# Revit family: ALM_клапан
name_source: partatom
category: Арматура воздуховодов
revit_build: Autodesk Revit 2014 (Build: 20140709_2115(x64)
units: mm (PartAtom-declared; Revit-internal decimal feet)

## types (198) — shared parameters
Aef = 0.82 м²
W = 70 мм
Материал = Оцинкованная сталь (INPLAST)
УГО = УГО(INPLAST)

## per-type parameters (varying)
| type | A | B | Вес | Тип привода |
| ALM-100x105-T1 | 100 мм | 105 мм | 0.7 | 1 |
| ALM-100x155-T1 | 100 мм | 155 мм | 0.9 | 1 |
| ALM-100x205-T1 | 100 мм | 205 мм | 1.2 | 1 |
| ALM-100x255-T1 | 100 мм | 255 мм | 1.4 | 1 |
| ALM-100x305-T1 | 100 мм | 305 мм | 1.6 | 1 |
| ALM-100x355-T1 | 100 мм | 355 мм | 1.9 | 1 |
| ALM-100x405-T1 | 100 мм | 405 мм | 2.1 | 1 |
| ALM-100x455-T1 | 100 мм | 455 мм | 2.4 | 1 |
| ALM-100x505-T1 | 100 мм | 505 мм | 2.6 | 1 |
| ALM-100x555-T1 | 100 мм | 555 мм | 2.9 | 1 |
| ALM-100x605-T1 | 100 мм | 605 мм | 3.1 | 1 |
| ALM-200x105-T1 | 200 мм | 105 мм | 0.8 | 1 |
| ALM-200x155-T1 | 200 мм | 155 мм | 1.1 | 1 |
| ALM-200x205-T1 | 200 мм | 205 мм | 1.4 | 1 |
| ALM-200x255-T1 | 200 мм | 255 мм | 1.7 | 1 |
| ALM-200x305-T1 | 200 мм | 305 мм | 1.9 | 1 |
| ALM-200x355-T1 | 200 мм | 355 мм | 2.2 | 1 |
| ALM-200x405-T1 | 200 мм | 405 мм | 2.5 | 1 |
| ALM-200x455-T1 | 200 мм | 455 мм | 2.8 | 1 |
| ALM-200x505-T1 | 200 мм | 505 мм | 3.1 | 1 |
| ALM-200x555-T1 | 200 мм | 555 мм | 3.4 | 1 |
| ALM-200x605-T1 | 200 мм | 605 мм | 3.7 | 1 |
| ALM-300x105-T1 | 300 мм | 105 мм | 1 | 1 |
| ALM-300x155-T1 | 300 мм | 155 мм | 1.3 | 1 |
| ALM-300x205-T1 | 300 мм | 205 мм | 1.6 | 1 |
| ALM-300x255-T1 | 300 мм | 255 мм | 1.9 | 1 |
| ALM-300x305-T1 | 300 мм | 305 мм | 2.3 | 1 |
| ALM-300x355-T1 | 300 мм | 355 мм | 2.6 | 1 |
| ALM-300x405-T1 | 300 мм | 405 мм | 2.9 | 1 |
| ALM-300x455-T1 | 300 мм | 455 мм | 3.3 | 1 |
| ALM-300x505-T1 | 300 мм | 505 мм | 3.6 | 1 |
| ALM-300x555-T1 | 300 мм | 555 мм | 3.9 | 1 |
| ALM-300x605-T1 | 300 мм | 605 мм | 4.2 | 1 |
| ALM-400x105-T1 | 400 мм | 105 мм | 1.1 | 1 |
| ALM-400x155-T1 | 400 мм | 155 мм | 1.5 | 1 |
| ALM-400x205-T1 | 400 мм | 205 мм | 1.9 | 1 |
| ALM-400x255-T1 | 400 мм | 255 мм | 2.2 | 1 |
| ALM-400x305-T1 | 400 мм | 305 мм | 2.6 | 1 |
| ALM-400x355-T1 | 400 мм | 355 мм | 2.9 | 1 |
| ALM-400x405-T1 | 400 мм | 405 мм | 3.3 | 1 |
| ALM-400x455-T1 | 400 мм | 455 мм | 3.7 | 1 |
| ALM-400x505-T1 | 400 мм | 505 мм | 4.1 | 1 |
| ALM-400x555-T1 | 400 мм | 555 мм | 4.4 | 1 |
| ALM-400x605-T1 | 400 мм | 605 мм | 4.8 | 1 |
| ALM-500x105-T1 | 500 мм | 105 мм | 1.3 | 1 |
| ALM-500x155-T1 | 500 мм | 155 мм | 1.7 | 1 |
| ALM-500x205-T1 | 500 мм | 205 мм | 2.1 | 1 |
| ALM-500x255-T1 | 500 мм | 255 мм | 2.5 | 1 |
| ALM-500x305-T1 | 500 мм | 305 мм | 2.9 | 1 |
| ALM-500x355-T1 | 500 мм | 355 мм | 3.3 | 1 |
| ALM-500x405-T1 | 500 мм | 405 мм | 3.7 | 1 |
| ALM-500x455-T1 | 500 мм | 455 мм | 4.1 | 1 |
| ALM-500x505-T1 | 500 мм | 505 мм | 4.5 | 1 |
| ALM-500x555-T1 | 500 мм | 555 мм | 4.9 | 1 |
| ALM-500x605-T1 | 500 мм | 605 мм | 5.3 | 1 |
| ALM-600x105-T1 | 600 мм | 105 мм | 1.4 | 1 |
| ALM-600x155-T1 | 600 мм | 155 мм | 1.9 | 1 |
| ALM-600x205-T1 | 600 мм | 205 мм | 2.3 | 1 |
| ALM-600x255-T1 | 600 мм | 255 мм | 2.8 | 1 |
| ALM-600x305-T1 | 600 мм | 305 мм | 3.2 | 1 |
| ALM-600x355-T1 | 600 мм | 355 мм | 3.7 | 1 |
| ALM-600x405-T1 | 600 мм | 405 мм | 4.1 | 1 |
| ALM-600x455-T1 | 600 мм | 455 мм | 4.6 | 1 |
| ALM-600x505-T1 | 600 мм | 505 мм | 5 | 1 |
| ALM-600x555-T1 | 600 мм | 555 мм | 5.5 | 1 |
| ALM-600x605-T1 | 600 мм | 605 мм | 5.9 | 1 |
| ALM-100x105-T2 | 100 мм | 105 мм | 0.7 | 2 |
| ALM-100x155-T2 | 100 мм | 155 мм | 0.9 | 2 |
| ALM-100x205-T2 | 100 мм | 205 мм | 1.2 | 2 |
| ALM-100x255-T2 | 100 мм | 255 мм | 1.4 | 2 |
| ALM-100x305-T2 | 100 мм | 305 мм | 1.6 | 2 |
| ALM-100x355-T2 | 100 мм | 355 мм | 1.9 | 2 |
| ALM-100x405-T2 | 100 мм | 405 мм | 2.1 | 2 |
| ALM-100x455-T2 | 100 мм | 455 мм | 2.4 | 2 |
| ALM-100x505-T2 | 100 мм | 505 мм | 2.6 | 2 |
| ALM-100x555-T2 | 100 мм | 555 мм | 2.9 | 2 |
| ALM-100x605-T2 | 100 мм | 605 мм | 3.1 | 2 |
| ALM-200x105-T2 | 200 мм | 105 мм | 0.8 | 2 |
| ALM-200x155-T2 | 200 мм | 155 мм | 1.1 | 2 |
| ALM-200x205-T2 | 200 мм | 205 мм | 1.4 | 2 |
| ALM-200x255-T2 | 200 мм | 255 мм | 1.7 | 2 |
| ALM-200x305-T2 | 200 мм | 305 мм | 1.9 | 2 |
| ALM-200x355-T2 | 200 мм | 355 мм | 2.2 | 2 |
| ALM-200x405-T2 | 200 мм | 405 мм | 2.5 | 2 |
| ALM-200x455-T2 | 200 мм | 455 мм | 2.8 | 2 |
| ALM-200x505-T2 | 200 мм | 505 мм | 3.1 | 2 |
| ALM-200x555-T2 | 200 мм | 555 мм | 3.4 | 2 |
| ALM-200x605-T2 | 200 мм | 605 мм | 3.7 | 2 |
| ALM-300x105-T2 | 300 мм | 105 мм | 1 | 2 |
| ALM-300x155-T2 | 300 мм | 155 мм | 1.3 | 2 |
| ALM-300x205-T2 | 300 мм | 205 мм | 1.6 | 2 |
| ALM-300x255-T2 | 300 мм | 255 мм | 1.9 | 2 |
| ALM-300x305-T2 | 300 мм | 305 мм | 2.3 | 2 |
| ALM-300x355-T2 | 300 мм | 355 мм | 2.6 | 2 |
| ALM-300x405-T2 | 300 мм | 405 мм | 2.9 | 2 |
| ALM-300x455-T2 | 300 мм | 455 мм | 3.3 | 2 |
| ALM-300x505-T2 | 300 мм | 505 мм | 3.6 | 2 |
| ALM-300x555-T2 | 300 мм | 555 мм | 3.9 | 2 |
| ALM-300x605-T2 | 300 мм | 605 мм | 4.2 | 2 |
| ALM-400x105-T2 | 400 мм | 105 мм | 1.1 | 2 |
| ALM-400x155-T2 | 400 мм | 155 мм | 1.5 | 2 |
| ALM-400x205-T2 | 400 мм | 205 мм | 1.9 | 2 |
| ALM-400x255-T2 | 400 мм | 255 мм | 2.2 | 2 |
| ALM-400x305-T2 | 400 мм | 305 мм | 2.6 | 2 |
| ALM-400x355-T2 | 400 мм | 355 мм | 2.9 | 2 |
| ALM-400x405-T2 | 400 мм | 405 мм | 3.3 | 2 |
| ALM-400x455-T2 | 400 мм | 455 мм | 3.7 | 2 |
| ALM-400x505-T2 | 400 мм | 505 мм | 4.1 | 2 |
| ALM-400x555-T2 | 400 мм | 555 мм | 4.4 | 2 |
| ALM-400x605-T2 | 400 мм | 605 мм | 4.8 | 2 |
| ALM-500x105-T2 | 500 мм | 105 мм | 1.3 | 2 |
| ALM-500x155-T2 | 500 мм | 155 мм | 1.7 | 2 |
| ALM-500x205-T2 | 500 мм | 205 мм | 2.1 | 2 |
| ALM-500x255-T2 | 500 мм | 255 мм | 2.5 | 2 |
| ALM-500x305-T2 | 500 мм | 305 мм | 2.9 | 2 |
| ALM-500x355-T2 | 500 мм | 355 мм | 3.3 | 2 |
| ALM-500x405-T2 | 500 мм | 405 мм | 3.7 | 2 |
| ALM-500x455-T2 | 500 мм | 455 мм | 4.1 | 2 |
| ALM-500x505-T2 | 500 мм | 505 мм | 4.5 | 2 |
| ALM-500x555-T2 | 500 мм | 555 мм | 4.9 | 2 |
| ALM-500x605-T2 | 500 мм | 605 мм | 5.3 | 2 |
| ALM-600x105-T2 | 600 мм | 105 мм | 1.4 | 2 |
| ALM-600x155-T2 | 600 мм | 155 мм | 1.9 | 2 |
| ALM-600x205-T2 | 600 мм | 205 мм | 2.3 | 2 |
| ALM-600x255-T2 | 600 мм | 255 мм | 2.8 | 2 |
| ALM-600x305-T2 | 600 мм | 305 мм | 3.2 | 2 |
| ALM-600x355-T2 | 600 мм | 355 мм | 3.7 | 2 |
| ALM-600x405-T2 | 600 мм | 405 мм | 4.1 | 2 |
| ALM-600x455-T2 | 600 мм | 455 мм | 4.6 | 2 |
| ALM-600x505-T2 | 600 мм | 505 мм | 5 | 2 |
| ALM-600x555-T2 | 600 мм | 555 мм | 5.5 | 2 |
| ALM-600x605-T2 | 600 мм | 605 мм | 5.9 | 2 |
| ALM-100x105-T3 | 100 мм | 105 мм | 0.7 | 3 |
| ALM-100x155-T3 | 100 мм | 155 мм | 0.9 | 3 |
| ALM-100x205-T3 | 100 мм | 205 мм | 1.2 | 3 |
| ALM-100x255-T3 | 100 мм | 255 мм | 1.4 | 3 |
| ALM-100x305-T3 | 100 мм | 305 мм | 1.6 | 3 |
| ALM-100x355-T3 | 100 мм | 355 мм | 1.9 | 3 |
| ALM-100x405-T3 | 100 мм | 405 мм | 2.1 | 3 |
| ALM-100x455-T3 | 100 мм | 455 мм | 2.4 | 3 |
| ALM-100x505-T3 | 100 мм | 505 мм | 2.6 | 3 |
| ALM-100x555-T3 | 100 мм | 555 мм | 2.9 | 3 |
| ALM-100x605-T3 | 100 мм | 605 мм | 3.1 | 3 |
| ALM-200x105-T3 | 200 мм | 105 мм | 0.8 | 3 |
| ALM-200x155-T3 | 200 мм | 155 мм | 1.1 | 3 |
| ALM-200x205-T3 | 200 мм | 205 мм | 1.4 | 3 |
| ALM-200x255-T3 | 200 мм | 255 мм | 1.7 | 3 |
| ALM-200x305-T3 | 200 мм | 305 мм | 1.9 | 3 |
| ALM-200x355-T3 | 200 мм | 355 мм | 2.2 | 3 |
| ALM-200x405-T3 | 200 мм | 405 мм | 2.5 | 3 |
| ALM-200x455-T3 | 200 мм | 455 мм | 2.8 | 3 |
| ALM-200x505-T3 | 200 мм | 505 мм | 3.1 | 3 |
| ALM-200x555-T3 | 200 мм | 555 мм | 3.4 | 3 |
| ALM-200x605-T3 | 200 мм | 605 мм | 3.7 | 3 |
| ALM-300x105-T3 | 300 мм | 105 мм | 1 | 3 |
| ALM-300x155-T3 | 300 мм | 155 мм | 1.3 | 3 |
| ALM-300x205-T3 | 300 мм | 205 мм | 1.6 | 3 |
| ALM-300x255-T3 | 300 мм | 255 мм | 1.9 | 3 |
| ALM-300x305-T3 | 300 мм | 305 мм | 2.3 | 3 |
| ALM-300x355-T3 | 300 мм | 355 мм | 2.6 | 3 |
| ALM-300x405-T3 | 300 мм | 405 мм | 2.9 | 3 |
| ALM-300x455-T3 | 300 мм | 455 мм | 3.3 | 3 |
| ALM-300x505-T3 | 300 мм | 505 мм | 3.6 | 3 |
| ALM-300x555-T3 | 300 мм | 555 мм | 3.9 | 3 |
| ALM-300x605-T3 | 300 мм | 605 мм | 4.2 | 3 |
| ALM-400x105-T3 | 400 мм | 105 мм | 1.1 | 3 |
| ALM-400x155-T3 | 400 мм | 155 мм | 1.5 | 3 |
| ALM-400x205-T3 | 400 мм | 205 мм | 1.9 | 3 |
| ALM-400x255-T3 | 400 мм | 255 мм | 2.2 | 3 |
| ALM-400x305-T3 | 400 мм | 305 мм | 2.6 | 3 |
| ALM-400x355-T3 | 400 мм | 355 мм | 2.9 | 3 |
| ALM-400x405-T3 | 400 мм | 405 мм | 3.3 | 3 |
| ALM-400x455-T3 | 400 мм | 455 мм | 3.7 | 3 |
| ALM-400x505-T3 | 400 мм | 505 мм | 4.1 | 3 |
| ALM-400x555-T3 | 400 мм | 555 мм | 4.4 | 3 |
| ALM-400x605-T3 | 400 мм | 605 мм | 4.8 | 3 |
| ALM-500x105-T3 | 500 мм | 105 мм | 1.3 | 3 |
| ALM-500x155-T3 | 500 мм | 155 мм | 1.7 | 3 |
| ALM-500x205-T3 | 500 мм | 205 мм | 2.1 | 3 |
| ALM-500x255-T3 | 500 мм | 255 мм | 2.5 | 3 |
| ALM-500x305-T3 | 500 мм | 305 мм | 2.9 | 3 |
| ALM-500x355-T3 | 500 мм | 355 мм | 3.3 | 3 |
| ALM-500x405-T3 | 500 мм | 405 мм | 3.7 | 3 |
| ALM-500x455-T3 | 500 мм | 455 мм | 4.1 | 3 |
| ALM-500x505-T3 | 500 мм | 505 мм | 4.5 | 3 |
| ALM-500x555-T3 | 500 мм | 555 мм | 4.9 | 3 |
| ALM-500x605-T3 | 500 мм | 605 мм | 5.3 | 3 |
| ALM-600x105-T3 | 600 мм | 105 мм | 1.4 | 3 |
| ALM-600x155-T3 | 600 мм | 155 мм | 1.9 | 3 |
| ALM-600x205-T3 | 600 мм | 205 мм | 2.3 | 3 |
| ALM-600x255-T3 | 600 мм | 255 мм | 2.8 | 3 |
| ALM-600x305-T3 | 600 мм | 305 мм | 3.2 | 3 |
| ALM-600x355-T3 | 600 мм | 355 мм | 3.7 | 3 |
| ALM-600x405-T3 | 600 мм | 405 мм | 4.1 | 3 |
| ALM-600x455-T3 | 600 мм | 455 мм | 4.6 | 3 |
| ALM-600x505-T3 | 600 мм | 505 мм | 5 | 3 |
| ALM-600x555-T3 | 600 мм | 555 мм | 5.5 | 3 |
| ALM-600x605-T3 | 600 мм | 605 мм | 5.9 | 3 |

note: column(s) folded — value = type name in every type: Комментарии к типоразмеру
